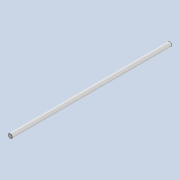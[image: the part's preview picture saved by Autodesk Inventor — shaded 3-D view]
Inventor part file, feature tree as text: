
AUTODESK INVENTOR PART (.ipt)
format: ipt  version: 2020 (Build 240168000, 168)  size: 79,360 bytes
history: native  units: mm
features: extrude x1, chamfer x1, sketch x1
ambient origin geometry x8: Origin, YZ Plane, XZ Plane, XY Plane, X Axis, Y Axis, Z Axis, Center Point
bodies: Solid1 (feature_tree)
feature tree (3):
  extrude  "Extrusion1"  Depth=377.0mm TaperAngle=0.0deg
  chamfer  "Chamfer1"  Distance=0.5mm Angle=45.0deg
  sketch  "Sketch1"  dims[d0=10.0mm d1=377.0mm d2=0.0mm d3=0.5mm d4=2.0mm d5=45.0deg]
